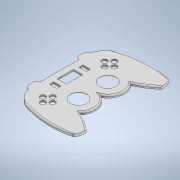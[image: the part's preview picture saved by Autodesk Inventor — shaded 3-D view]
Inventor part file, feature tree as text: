
AUTODESK INVENTOR PART (.ipt)
format: ipt  version: 2022 (Build 260153000, 153)  size: 489,984 bytes
history: native  units: mm
features: sketch x4, extrude x3, fillet x2
ambient origin geometry x8: Origin, YZ Plane, XZ Plane, XY Plane, X Axis, Y Axis, Z Axis, Center Point
bodies: Solid1 (feature_tree)
feature tree (9):
  sketch  "Sketch1"  dims[d0=35.0mm d1=60.0mm]
  extrude  "Extrusion1"  Depth=60.0mm
  extrude  "Extrusion2"  Depth=25.0mm
  extrude  "Extrusion4"  Depth=25.0mm
  fillet  "Fillet3"  Radius=27.0mm
  fillet  "Fillet4"  Radius=34.0mm
  sketch  "Sketch2"  dims[d2=17.5mm d3=25.0mm]
  sketch  "Sketch4"  dims[d4=22.5mm d6=25.0mm d7=27.0mm d8=34.0mm]
  sketch  "Sketch6"  dims[d9=27.0mm d10=7.5mm d11=25.0mm d12=27.0mm d13=34.0mm d14=27.0mm d15=6.0mm d16=6.0mm d17=6.0mm d18=6.5mm d22=6.0mm d23=40.0mm d25=360.0deg d27=25.0mm d28=27.0mm d31=40.0mm d32=25.0mm d33=27.0mm d34=5.0mm d35=8.0mm d36=8.0mm d58=40.0mm d60=360.0deg d62=50.0mm d63=2.0mm d64=0.0mm d70=13.425896mm d72=37.3mm d73=4.0mm d74=37.3mm d86=6.5mm d93=0.5mm d95=40.0mm d97=40.0mm d98=2.0mm d99=0.0mm d104=15.0mm d105=15.0mm d106=15.0mm d107=15.0mm d108=30.0mm d109=25.0mm d110=22.75mm d111=0.25mm d113=25.0mm d114=5.0mm d115=5.0mm d116=2.5mm d117=5.0mm d118=5.0mm d119=40.0mm d121=360.0deg d123=22.5mm d124=1.5mm d125=8.0mm d126=12.5mm d127=14.0mm d128=25.0mm d129=8.0mm d130=8.0mm d131=8.0mm d132=8.0mm d133=5.0mm d134=0.0mm d135=7.0mm d136=1.5mm d137=6.0mm d139=6.5mm d140=11.0mm d141=2.0mm d142=2.0mm]
